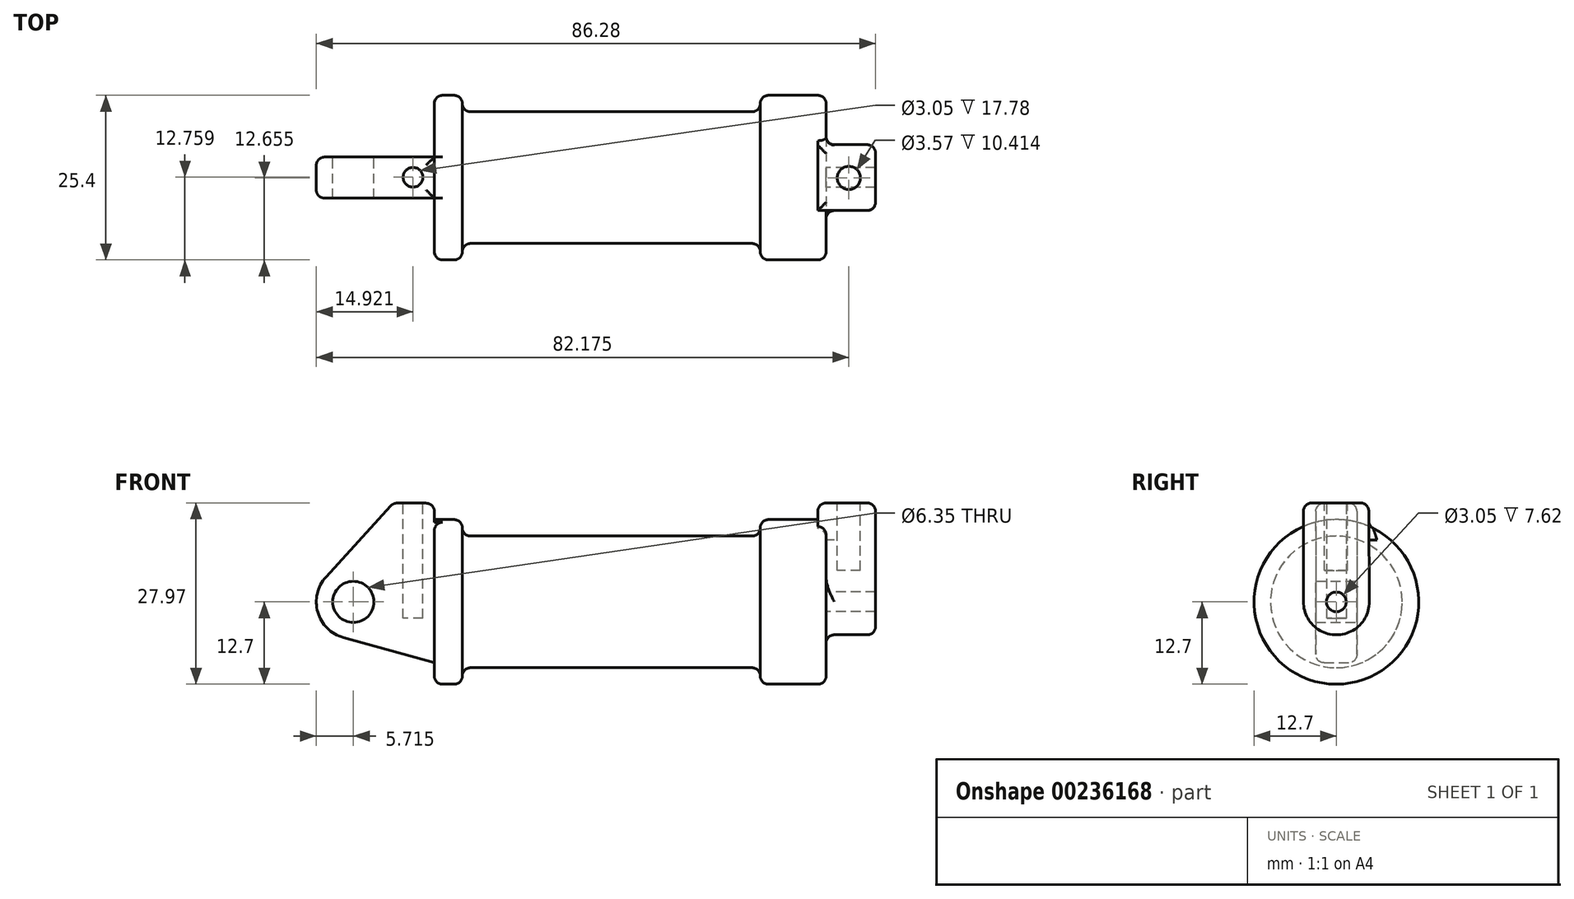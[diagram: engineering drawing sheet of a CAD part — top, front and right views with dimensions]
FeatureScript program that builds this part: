
annotation { "Feature Type Name" : "Feature", "Feature Type Description" : "" }
export const myFeature = defineFeature(function(context is Context, id is Id, definition is map)
    precondition{}
    {
        {
            var Q0;
            Q0=qCreatedBy(makeId("Front.planeOp"),FACE);
            var sketch = newSketch(context, id + "F0", { "sketchPlane" : qUnion([Q0])});
            skLineSegment(sketch, "E0", {"start": v(0, 0) * mm, "end": v(0, 12.7) * mm});
            skLineSegment(sketch, "E1", {"start": v(0, 12.7) * mm, "end": v(10.16, 12.7) * mm});
            skLineSegment(sketch, "E2", {"start": v(10.16, 12.7) * mm, "end": v(10.16, 10.16) * mm});
            skLineSegment(sketch, "E3", {"start": v(10.16, 10.16) * mm, "end": v(56.13, 10.16) * mm});
            skLineSegment(sketch, "E4", {"start": v(56.13, 10.16) * mm, "end": v(56.13, 12.7) * mm});
            skLineSegment(sketch, "E5", {"start": v(56.13, 12.7) * mm, "end": v(66.3, 12.7) * mm});
            skLineSegment(sketch, "E6", {"start": v(66.3, 12.7) * mm, "end": v(66.3, 0) * mm});
            skLineSegment(sketch, "E7", {"start": v(66.3, 0) * mm, "end": v(0, 0) * mm});
            skLineSegment(sketch, "E8", {"start": v(5.84, 15.24) * mm, "end": v(-0.5, 15.24) * mm});
            skLineSegment(sketch, "E9", {"start": v(-0.5, 15.24) * mm, "end": v(-10.88, 3.85) * mm});
            skLineSegment(sketch, "E10", {"start": v(0, 0) * mm, "end": v(-6.65, 0) * mm});
            skCircle(sketch, "E11", {"center": v(-6.65, 0) * mm, "radius": 5.72 * mm});
            skCircle(sketch, "E12", {"center": v(-6.65, 0) * mm, "radius": 3.18 * mm});
            skLineSegment(sketch, "E13", {"start": v(5.84, 15.24) * mm, "end": v(5.84, -9.4) * mm});
            skLineSegment(sketch, "E14", {"start": v(5.84, -9.4) * mm, "end": v(-8.18, -5.5) * mm});
            skSolve(sketch);
        }
        {
            var Q0;
            {var subQ0=sQuery(id+"F0.wireOp",EDGE,"E2");Q0=makeQuery(id+"F0.imprint","IMPRINT",FACE,{"disambiguationData":[TD([[makeQuery(id+"F0.imprint","IMPRINT",EDGE,{"derivedFrom":subQ0}),-1.0]])]});}
            var Q1;
            Q1=sQuery(id+"F0.wireOp",EDGE,"E7");
            revolve(context, id + "F1", {"entities" : qUnion([Q0]), "axis" : qUnion([Q1]), "revolveType" : RevolveType.FULL});
        }
        {
            var Q0;
            {var subQ0=sQuery(id+"F0.wireOp",EDGE,"E0");Q0=makeQuery(id+"F0.imprint","IMPRINT",FACE,{"disambiguationData":[TD([[makeQuery(id+"F0.imprint","IMPRINT",EDGE,{"derivedFrom":subQ0}),-1.0]])]});}
            var Q1;
            {var subQ0=sQuery(id+"F0.wireOp",EDGE,"E14");Q1=makeQuery(id+"F0.imprint","IMPRINT",FACE,{"disambiguationData":[TD([[makeQuery(id+"F0.imprint","IMPRINT",EDGE,{"derivedFrom":subQ0}),-1.0]])]});}
            var Q2;
            {var subQ3=sQuery(id+"F0.wireOp",EDGE,"E0");Q2=makeQuery(id+"F0.imprint","IMPRINT",FACE,{"disambiguationData":[TD([[makeQuery(id+"F0.imprint","IMPRINT",EDGE,{"derivedFrom":subQ3}),1.0]])]});}
            var Q3;
            {var subQ4=sQuery(id+"F0.wireOp",EDGE,"E12");Q3=makeQuery(id+"F0.imprint","IMPRINT",FACE,{"disambiguationData":[TD([[makeQuery(id+"F0.imprint","IMPRINT",EDGE,{"derivedFrom":subQ4}),-1.0]])]});}
            extrude(context, id + "F2", {"entities" : qUnion([Q0, Q1, Q2, Q3]), "operationType" : NewBodyOperationType.ADD, "endBound" : BoundingType.SYMMETRIC, "depth" : 6.35 * mm});
        }
        {
            var Q0;
            Q0=makeQuery(id+"F1.opRevolve","SWEPT_FACE",FACE,{"disambiguationData":[OSD([sQuery(id+"F0.wireOp",EDGE,"E6")])]});
            var sketch = newSketch(context, id + "F3", { "sketchPlane" : qUnion([Q0])});
            skCircle(sketch, "E15", {"center": v(0, 0) * mm, "radius": 1.52 * mm});
            skCircle(sketch, "E16", {"center": v(0, 0) * mm, "radius": 5.08 * mm});
            skLineSegment(sketch, "E17", {"start": v(-5.08, 0.03) * mm, "end": v(-5.08, 15.27) * mm});
            skLineSegment(sketch, "E18", {"start": v(-5.08, 15.27) * mm, "end": v(5, 15.27) * mm});
            skLineSegment(sketch, "E19", {"start": v(5, 15.27) * mm, "end": v(5.08, 0.03) * mm});
            skSolve(sketch);
        }
        {
            var Q0;
            {var subQ0=sQuery(id+"F3.wireOp",EDGE,"E18");Q0=makeQuery(id+"F3.imprint","IMPRINT",FACE,{"disambiguationData":[TD([[makeQuery(id+"F3.imprint","IMPRINT",EDGE,{"derivedFrom":subQ0}),-1.0]])]});}
            var Q1;
            {var subQ0=sQuery(id+"F3.wireOp",EDGE,"E17");var subQ1=sQuery(id+"F3.wireOp",EDGE,"E16");var subQ2=makeQuery(id+"F3.imprint","INTERSECT",VERTEX,{"derivedFrom":[subQ1,subQ0]});Q1=makeQuery(id+"F3.imprint","IMPRINT",FACE,{"disambiguationData":[TD([[makeQuery(id+"F3.imprint","IMPRINT",EDGE,{"disambiguationData":[TD([[subQ2,1.0]])],"derivedFrom":subQ1}),-1.0]])]});}
            var Q2;
            Q2=makeQuery(id+"F3.imprint","IMPRINT",FACE,{"disambiguationData":[TD([[makeQuery(id+"F3.imprint","IMPRINT",EDGE,{"derivedFrom":sQuery(id+"F3.wireOp",EDGE,"E15")}),-1.0]])]});
            extrude(context, id + "F4", {"entities" : qUnion([Q0, Q1, Q2]), "operationType" : NewBodyOperationType.ADD, "depth" : 7.62 * mm});
        }
        {
            var Q0;
            {var subQ0=sQuery(id+"F3.wireOp",EDGE,"E18");Q0=makeQuery(id+"F3.imprint","IMPRINT",FACE,{"disambiguationData":[TD([[makeQuery(id+"F3.imprint","IMPRINT",EDGE,{"derivedFrom":subQ0}),-1.0]])]});}
            var Q1;
            {var subQ0=sQuery(id+"F3.wireOp",EDGE,"E17");var subQ1=sQuery(id+"F3.wireOp",EDGE,"E16");var subQ2=makeQuery(id+"F3.imprint","INTERSECT",VERTEX,{"derivedFrom":[subQ1,subQ0]});Q1=makeQuery(id+"F3.imprint","IMPRINT",FACE,{"disambiguationData":[TD([[makeQuery(id+"F3.imprint","IMPRINT",EDGE,{"disambiguationData":[TD([[subQ2,1.0]])],"derivedFrom":subQ1}),-1.0]])]});}
            var Q2;
            Q2=makeQuery(id+"F3.imprint","IMPRINT",FACE,{"disambiguationData":[TD([[makeQuery(id+"F3.imprint","IMPRINT",EDGE,{"derivedFrom":sQuery(id+"F3.wireOp",EDGE,"E15")}),-1.0]])]});
            extrude(context, id + "F5", {"entities" : qUnion([Q0, Q1, Q2]), "operationType" : NewBodyOperationType.ADD, "oppositeDirection" : true, "depth" : 1.27 * mm});
        }
        {
            var Q0;
            Q0=makeQuery(id+"F2.opExtrude","SWEPT_FACE",FACE,{"disambiguationData":[OSD([sQuery(id+"F0.wireOp",EDGE,"E8")])]});
            var sketch = newSketch(context, id + "F6", { "sketchPlane" : qUnion([Q0])});
            skCircle(sketch, "E20", {"center": v(2.55, 0.06) * mm, "radius": 1.52 * mm});
            skSolve(sketch);
        }
        {
            var Q0;
            Q0 = qSketchRegion(id + "F6", true);
            extrude(context, id + "F7", {"entities" : qUnion([Q0]), "operationType" : NewBodyOperationType.REMOVE, "oppositeDirection" : true, "depth" : 17.78 * mm});
        }
        {
            var Q0;
            {var subQ0=sQuery(id+"F3.wireOp",EDGE,"E18");Q0=makeQuery(id+"F5.boolean.opBoolean","MERGE",FACE,{"derivedFrom":[makeQuery(id+"F4.opExtrude","SWEPT_FACE",FACE,{"disambiguationData":[OSD([subQ0])]}),makeQuery(id+"F5.opExtrude","SWEPT_FACE",FACE,{"disambiguationData":[OSD([subQ0])]})]});}
            var sketch = newSketch(context, id + "F8", { "sketchPlane" : qUnion([Q0])});
            skCircle(sketch, "E21", {"center": v(69.8, -0.04) * mm, "radius": 1.79 * mm});
            skPoint(sketch, "E21.centerSnap0", {"position": v(65.02, -0.04) * mm});
            skSolve(sketch);
        }
        {
            var Q0;
            Q0 = qSketchRegion(id + "F8", true);
            extrude(context, id + "F9", {"entities" : qUnion([Q0]), "operationType" : NewBodyOperationType.REMOVE, "oppositeDirection" : true, "depth" : 10.4 * mm});
        }
        {
            var Q0;
            Q0=makeQuery(id+"F1.opRevolve","SWEPT_EDGE",EDGE,{"disambiguationData":[OSD([sQuery(id+"F0.wireOp",EDGE,"E1"),sQuery(id+"F0.wireOp",EDGE,"E2")])]});
            var Q1;
            Q1=makeQuery(id+"F2.opExtrude","SWEPT_EDGE",EDGE,{"disambiguationData":[OSD([sQuery(id+"F0.wireOp",EDGE,"E8"),sQuery(id+"F0.wireOp",EDGE,"E13")])]});
            var Q2;
            Q2=makeQuery(id+"F1.opRevolve","SWEPT_EDGE",EDGE,{"disambiguationData":[OSD([sQuery(id+"F0.wireOp",EDGE,"E2"),sQuery(id+"F0.wireOp",EDGE,"E3")])]});
            var Q3;
            Q3=makeQuery(id+"F2.opExtrude","CAP_EDGE",EDGE,{"disambiguationData":[OSD([sQuery(id+"F0.wireOp",EDGE,"E8")])],"isStart":false});
            var Q4;
            Q4=makeQuery(id+"F2.opExtrude","SWEPT_EDGE",EDGE,{"disambiguationData":[OSD([sQuery(id+"F0.wireOp",EDGE,"E8"),sQuery(id+"F0.wireOp",EDGE,"E9")])]});
            var Q5;
            Q5=makeQuery(id+"F2.opExtrude","CAP_EDGE",EDGE,{"disambiguationData":[OSD([sQuery(id+"F0.wireOp",EDGE,"E8")])],"isStart":true});
            var Q6;
            Q6=makeQuery(id+"F2.opExtrude","CAP_EDGE",EDGE,{"disambiguationData":[OSD([sQuery(id+"F0.wireOp",EDGE,"E9")])],"isStart":false});
            var Q7;
            Q7=makeQuery(id+"F2.opExtrude","CAP_EDGE",EDGE,{"disambiguationData":[OSD([sQuery(id+"F0.wireOp",EDGE,"E9")])],"isStart":true});
            var Q8;
            Q8=makeQuery(id+"F2.opExtrude","CAP_EDGE",EDGE,{"disambiguationData":[OSD([sQuery(id+"F0.wireOp",EDGE,"E14")])],"isStart":true});
            var Q9;
            Q9=makeQuery(id+"F2.opExtrude","CAP_EDGE",EDGE,{"disambiguationData":[OSD([sQuery(id+"F0.wireOp",EDGE,"E11")])],"isStart":true});
            var Q10;
            Q10=makeQuery(id+"F2.opExtrude","SWEPT_FACE",FACE,{"disambiguationData":[OSD([sQuery(id+"F0.wireOp",EDGE,"E9")])]});
            var Q11;
            Q11=makeQuery(id+"F1.opRevolve","SWEPT_EDGE",EDGE,{"disambiguationData":[OSD([sQuery(id+"F0.wireOp",EDGE,"E4"),sQuery(id+"F0.wireOp",EDGE,"E5")])]});
            var Q12;
            Q12=makeQuery(id+"F1.opRevolve","SWEPT_EDGE",EDGE,{"disambiguationData":[OSD([sQuery(id+"F0.wireOp",EDGE,"E3"),sQuery(id+"F0.wireOp",EDGE,"E4")])]});
            var Q13;
            Q13=makeQuery(id+"F5.opExtrude","CAP_EDGE",EDGE,{"disambiguationData":[OSD([sQuery(id+"F3.wireOp",EDGE,"E18")])],"isStart":false});
            var Q14;
            {var subQ0=sQuery(id+"F3.wireOp",EDGE,"E19");var subQ1=sQuery(id+"F3.wireOp",EDGE,"E18");Q14=makeQuery(id+"F5.boolean.opBoolean","MERGE",EDGE,{"derivedFrom":[makeQuery(id+"F4.opExtrude","SWEPT_EDGE",EDGE,{"disambiguationData":[OSD([subQ1,subQ0])]}),makeQuery(id+"F5.opExtrude","SWEPT_EDGE",EDGE,{"disambiguationData":[OSD([subQ1,subQ0])]})]});}
            var Q15;
            {var subQ0=sQuery(id+"F0.wireOp",EDGE,"E5");var subQ1=sQuery(id+"F0.wireOp",EDGE,"E6");Q15=makeQuery(id+"F4.boolean.opBoolean","SPLIT",EDGE,{"disambiguationData":[topologyDisambiguationEdgeConnected([makeQuery(id+"F1.opRevolve","SWEPT_FACE",FACE,{"disambiguationData":[OSD([subQ1])]})])],"derivedFrom":makeQuery(id+"F1.opRevolve","SWEPT_EDGE",EDGE,{"disambiguationData":[OSD([subQ0,subQ1])]})});}
            var Q16;
            Q16=makeQuery(id+"F4.opExtrude","CAP_EDGE",EDGE,{"disambiguationData":[OSD([sQuery(id+"F3.wireOp",EDGE,"E18")])],"isStart":false});
            var Q17;
            {var subQ0=sQuery(id+"F3.wireOp",EDGE,"E18");var subQ1=sQuery(id+"F3.wireOp",EDGE,"E17");Q17=makeQuery(id+"F5.boolean.opBoolean","MERGE",EDGE,{"derivedFrom":[makeQuery(id+"F4.opExtrude","SWEPT_EDGE",EDGE,{"disambiguationData":[OSD([subQ1,subQ0])]}),makeQuery(id+"F5.opExtrude","SWEPT_EDGE",EDGE,{"disambiguationData":[OSD([subQ1,subQ0])]})]});}
            var Q18;
            Q18=makeQuery(id+"F4.opExtrude","CAP_EDGE",EDGE,{"disambiguationData":[OSD([sQuery(id+"F3.wireOp",EDGE,"E19")])],"isStart":false});
            var Q19;
            Q19=makeQuery(id+"F4.opExtrude","CAP_EDGE",EDGE,{"disambiguationData":[OSD([sQuery(id+"F3.wireOp",EDGE,"E16")])],"isStart":false});
            var Q20;
            Q20=makeQuery(id+"F4.opExtrude","CAP_EDGE",EDGE,{"disambiguationData":[OSD([sQuery(id+"F3.wireOp",EDGE,"E17")])],"isStart":false});
            var Q21;
            Q21=makeQuery(id+"F4.opExtrude","CAP_EDGE",EDGE,{"disambiguationData":[OSD([sQuery(id+"F3.wireOp",EDGE,"E16")])],"isStart":true});
            var Q22;
            {var subQ0=sQuery(id+"F0.wireOp",EDGE,"E1");var subQ1=sQuery(id+"F0.wireOp",EDGE,"E13");Q22=makeQuery(id+"F2.boolean.opBoolean","SPLIT",EDGE,{"disambiguationData":[topologyDisambiguationEdgeConnected([makeQuery(id+"F1.opRevolve","SWEPT_FACE",FACE,{"disambiguationData":[OSD([subQ1])]})])],"derivedFrom":makeQuery(id+"F1.opRevolve","SWEPT_EDGE",EDGE,{"disambiguationData":[OSD([subQ0,subQ1])]})});}
            fillet(context, id + "F10", {"entities" : qUnion([Q0, Q1, Q2, Q3, Q4, Q5, Q6, Q7, Q8, Q9, Q10, Q11, Q12, Q13, Q14, Q15, Q16, Q17, Q18, Q19, Q20, Q21, Q22]), "radius" : 1.27 * mm, "tangentPropagation" : true, "allowEdgeOverflow" : false});
        }
    });
